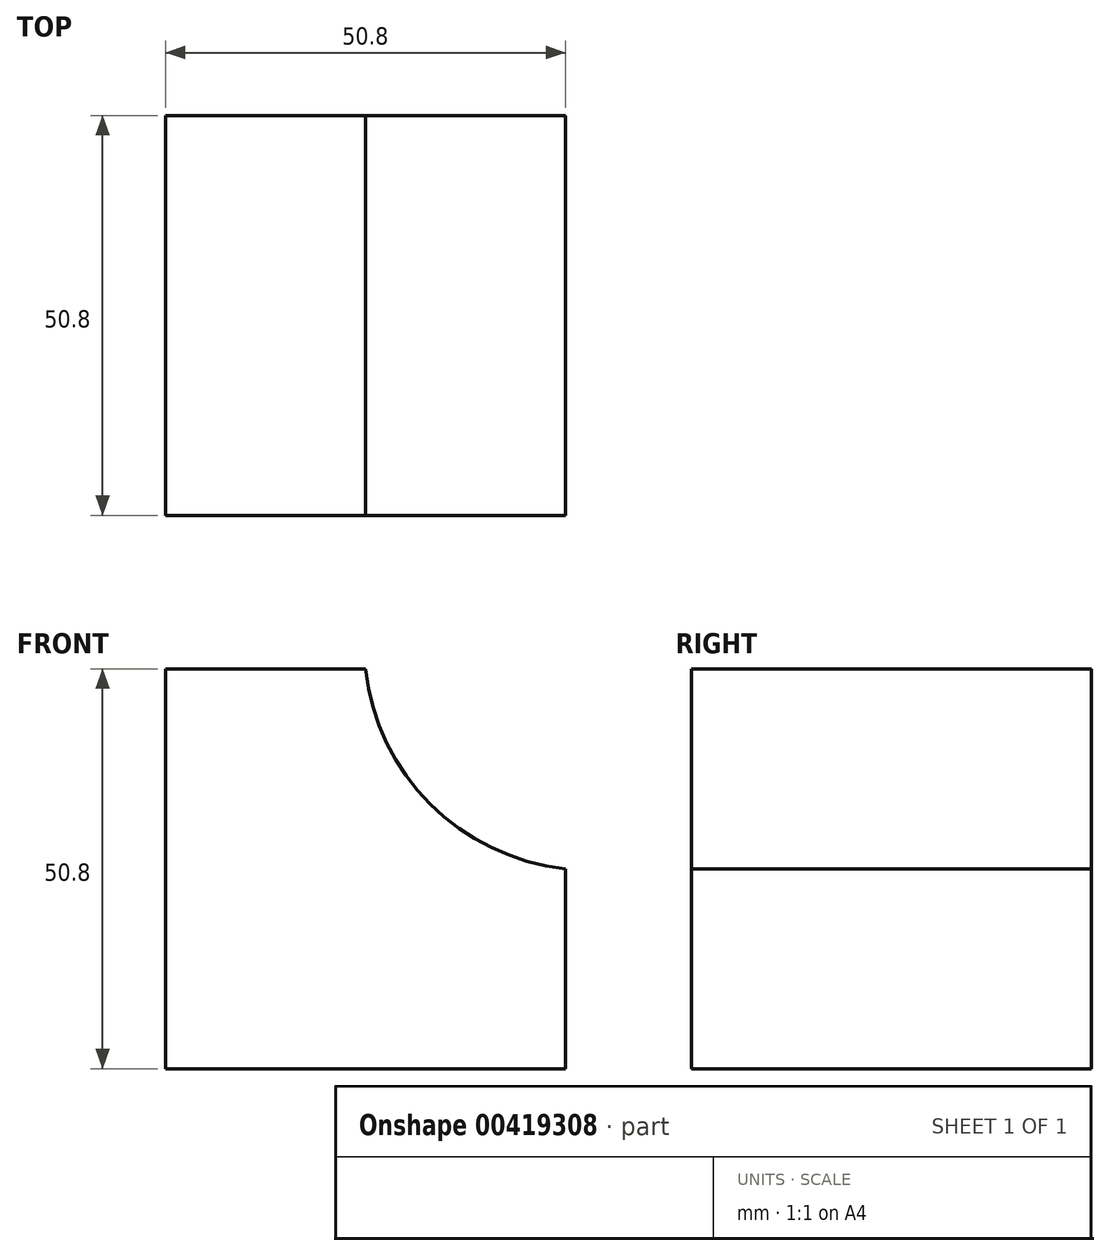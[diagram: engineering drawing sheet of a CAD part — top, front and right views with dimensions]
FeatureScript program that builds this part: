
annotation { "Feature Type Name" : "Feature", "Feature Type Description" : "" }
export const myFeature = defineFeature(function(context is Context, id is Id, definition is map)
    precondition{}
    {
        {
            var Q0;
            Q0=qCreatedBy(makeId("Front.planeOp"),FACE);
            var sketch = newSketch(context, id + "F0", { "sketchPlane" : qUnion([Q0])});
            skLineSegment(sketch, "E0", {"start": v(0, 0) * mm, "end": v(-50.8, 0) * mm});
            skLineSegment(sketch, "E1", {"start": v(-50.8, 0) * mm, "end": v(-50.8, 50.8) * mm});
            skLineSegment(sketch, "E2", {"start": v(-50.8, 50.8) * mm, "end": v(-25.4, 50.8) * mm});
            skLineSegment(sketch, "E3", {"start": v(0, 0) * mm, "end": v(0, 25.4) * mm});
            skArc(sketch, "E4", {"start": v(0, 25.4) * mm, "mid": v(-17.19, 33.61) * mm, "end": v(-25.4, 50.8) * mm});
            skSolve(sketch);
        }
        {
            var Q0;
            Q0=makeQuery(id+"F0.imprint","IMPRINT",FACE,{"disambiguationData":[TD([[makeQuery(id+"F0.imprint","IMPRINT",EDGE,{"derivedFrom":sQuery(id+"F0.wireOp",EDGE,"E0")}),-1.0]])]});
            extrude(context, id + "F1", {"entities" : qUnion([Q0]), "depth" : 50.8 * mm});
        }
    });
